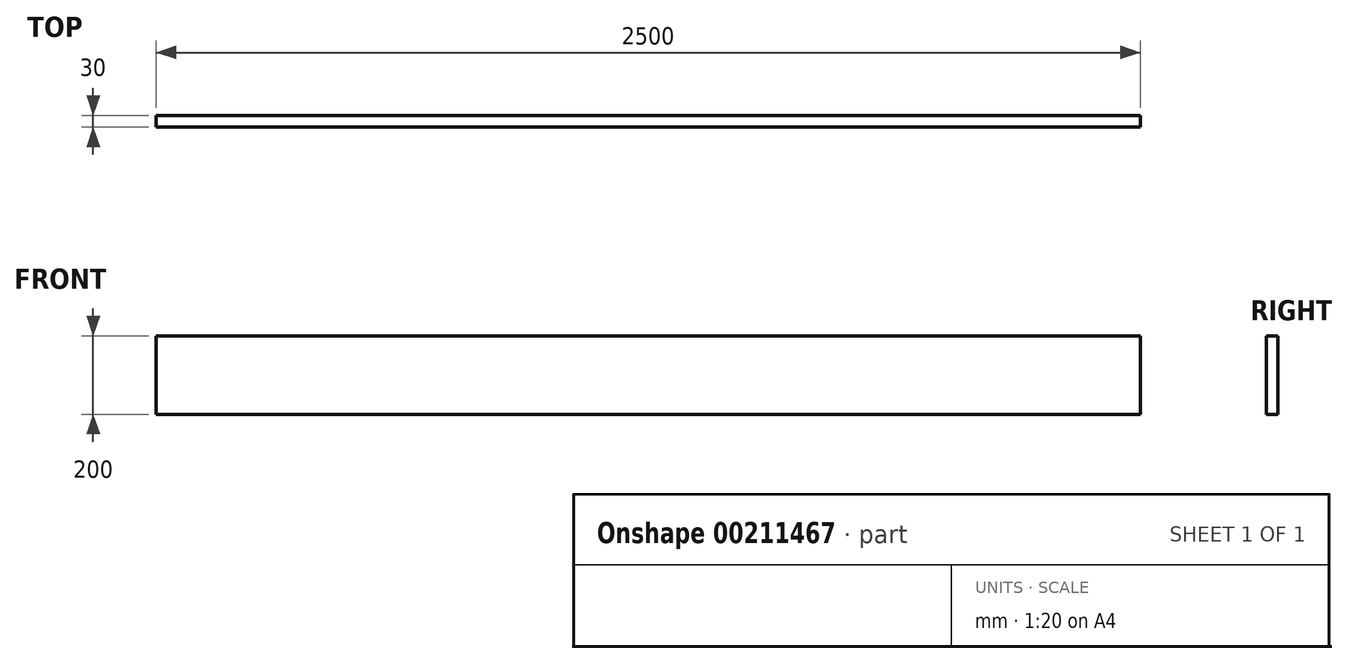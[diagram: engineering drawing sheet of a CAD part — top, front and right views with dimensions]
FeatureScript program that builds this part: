
annotation { "Feature Type Name" : "Feature", "Feature Type Description" : "" }
export const myFeature = defineFeature(function(context is Context, id is Id, definition is map)
    precondition{}
    {
        {
            var Q0;
            Q0=qCreatedBy(makeId("Front.planeOp"),FACE);
            var sketch = newSketch(context, id + "F0", { "sketchPlane" : qUnion([Q0])});
            skLineSegment(sketch, "E0.bottom", {"start": v(1250, 100) * mm, "end": v(-1250, 100) * mm});
            skLineSegment(sketch, "E0.top", {"start": v(1250, -100) * mm, "end": v(-1250, -100) * mm});
            skLineSegment(sketch, "E0.left", {"start": v(1250, 100) * mm, "end": v(1250, -100) * mm});
            skLineSegment(sketch, "E0.right", {"start": v(-1250, 100) * mm, "end": v(-1250, -100) * mm});
            skPoint(sketch, "E0.middle", {"position": v(0, 0) * mm});
            skSolve(sketch);
        }
        {
            var Q0;
            Q0=qSketchRegion(id+"F0",true);
            extrude(context, id + "F1", {"entities" : qUnion([Q0]), "depth" : 30 * mm});
        }
    });
